# Revit family: SLS-6712
name_source: partatom
category: Plumbing Fixtures
units: mm (PartAtom-declared; Revit-internal decimal feet)

## family parameters
Cut with Voids When Loaded = No
Host = Face
OmniClass Number = 23.65.70.11.11
OmniClass Title = Fixtures for Liquids
Part Type = Normal
Room Calculation Point = No
Round Connector Dimension = Use Diameter
Shared = No

## types (6) — shared parameters
CW Connection = No
HW Connection = No
Vent Connection = No
Waste Connection = No
z Has Rebuild Kit Trim Only = No
z Has Trim = No
zero-valued in all types: Default Elevation

## per-type parameters (varying)
| type | Gallons Per Minute | Product Material |
| 0.5 GPM Flow Restrictor, Polished Chrome | 0.500 GPM | Chrome - Symmons - Polished |
| 0.5 GPM Flow Restrictor, Satin Nickel | 0.500 GPM | Nickel - Symmons - Satin |
| 1.0 GPM Flow Restrictor, Satin Nickel | 1.000 GPM | Nickel - Symmons - Satin |
| 1.5 GPM Flow Restrictor, Satin Nickel | 1.500 GPM | Nickel - Symmons - Satin |
| 1.0 GPM Flow Restrictor, Polished Chrome | 1.000 GPM | Chrome - Symmons - Polished |
| 1.5 GPM Flow Restrictor, Polished Chrome | 1.500 GPM | Chrome - Symmons - Polished |

## geometry (parser evidence)
native form markers: Blend x2, Sweep x2
no freeform markers — native parametric forms only
